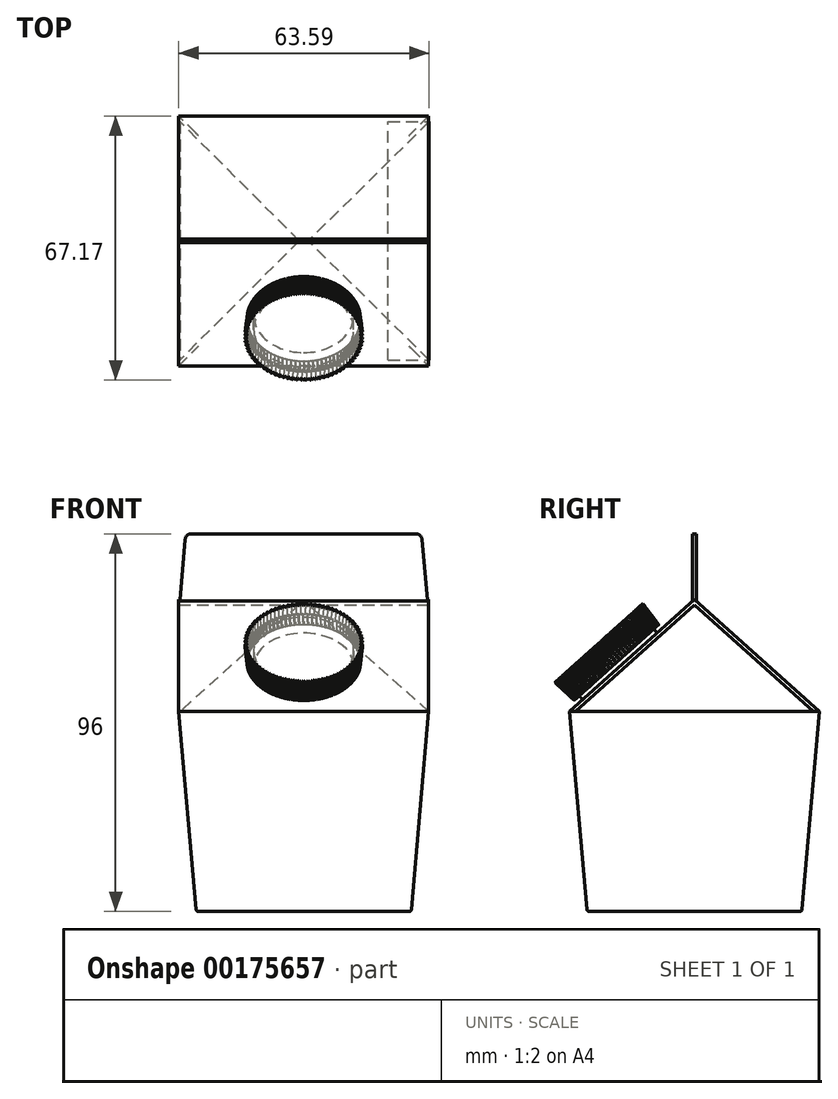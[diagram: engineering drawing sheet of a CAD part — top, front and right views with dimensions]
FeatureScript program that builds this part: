
annotation { "Feature Type Name" : "Feature", "Feature Type Description" : "" }
export const myFeature = defineFeature(function(context is Context, id is Id, definition is map)
    precondition{}
    {
        {
            var Q0;
            Q0=qCreatedBy(makeId("Top.planeOp"),FACE);
            var sketch = newSketch(context, id + "F0", { "sketchPlane" : qUnion([Q0])});
            skLineSegment(sketch, "E0.bottom", {"start": v(27.3, -27.3) * mm, "end": v(-27.3, -27.3) * mm});
            skLineSegment(sketch, "E0.top", {"start": v(27.3, 27.3) * mm, "end": v(-27.3, 27.3) * mm});
            skLineSegment(sketch, "E0.left", {"start": v(27.3, -27.3) * mm, "end": v(27.3, 27.3) * mm});
            skLineSegment(sketch, "E0.right", {"start": v(-27.3, -27.3) * mm, "end": v(-27.3, 27.3) * mm});
            skPoint(sketch, "E0.middle", {"position": v(0, 0) * mm});
            skSolve(sketch);
        }
        {
            var Q0;
            Q0=makeQuery(id+"F0.imprint","IMPRINT",FACE,{"disambiguationData":[TD([[makeQuery(id+"F0.imprint","IMPRINT",EDGE,{"derivedFrom":sQuery(id+"F0.wireOp",EDGE,"E0.bottom")}),-1.0]])]});
            extrude(context, id + "F1", {"entities" : qUnion([Q0]), "depth" : 50.8 * mm, "hasDraft" : true, "draftAngle" : 5 * degree});
        }
        {
            var Q0;
            Q0=qCreatedBy(makeId("Right.planeOp"),FACE);
            var sketch = newSketch(context, id + "F2", { "sketchPlane" : qUnion([Q0])});
            skLineSegment(sketch, "E1.0", {"start": v(-31.75, 50.8) * mm, "end": v(31.75, 50.8) * mm});
            skLineSegment(sketch, "E2", {"start": v(-27.4, 103.81) * mm, "end": v(78.6, 8.81) * mm, "construction": true});
            skLineSegment(sketch, "E3", {"start": v(0, -61.41) * mm, "end": v(0, 100.05) * mm, "construction": true});
            skLineSegment(sketch, "E4", {"start": v(31.75, 50.8) * mm, "end": v(0, 79.26) * mm, "construction": true});
            skPoint(sketch, "E4.endSnap0", {"position": v(0, 50.8) * mm});
            skLineSegment(sketch, "E5", {"start": v(0, 79.26) * mm, "end": v(-31.75, 50.8) * mm});
            skLineSegment(sketch, "E6", {"start": v(31.75, 50.8) * mm, "end": v(0, 79.26) * mm});
            skSolve(sketch);
        }
        {
            var Q0;
            Q0=makeQuery(id+"F2.imprint","IMPRINT",FACE,{"disambiguationData":[TD([[makeQuery(id+"F2.imprint","IMPRINT",EDGE,{"derivedFrom":sQuery(id+"F2.wireOp",EDGE,"E1.0")}),1.0]])]});
            extrude(context, id + "F3", {"entities" : qUnion([Q0]), "operationType" : NewBodyOperationType.ADD, "endBound" : BoundingType.SYMMETRIC, "depth" : 63.5 * mm});
        }
        {
            var Q0;
            Q0=makeQuery(id+"F3.opExtrude","CAP_FACE",FACE,{"disambiguationData":[OSD([sQuery(id+"F2.wireOp",EDGE,"E1.0"),sQuery(id+"F2.wireOp",EDGE,"E5"),sQuery(id+"F2.wireOp",EDGE,"E6")])],"isStart":false});
            var sketch = newSketch(context, id + "F4", { "sketchPlane" : qUnion([Q0])});
            skLineSegment(sketch, "E7", {"start": v(0, 28.77) * mm, "end": v(0, 80.29) * mm, "construction": true});
            skLineSegment(sketch, "E8.0", {"start": v(0, 77.96) * mm, "end": v(-30.3, 50.8) * mm});
            skLineSegment(sketch, "E8.1", {"start": v(30.3, 50.8) * mm, "end": v(0, 77.96) * mm});
            skLineSegment(sketch, "E9", {"start": v(-30.3, 50.8) * mm, "end": v(30.3, 50.8) * mm});
            skLineSegment(sketch, "E10", {"start": v(-17.16, 67.72) * mm, "end": v(-18, 68.66) * mm});
            skSolve(sketch);
        }
        {
            var Q0;
            Q0=makeQuery(id+"F4.imprint","IMPRINT",FACE,{"disambiguationData":[TD([[makeQuery(id+"F4.imprint","IMPRINT",EDGE,{"derivedFrom":sQuery(id+"F4.wireOp",EDGE,"E8.0")}),1.0]])]});
            extrude(context, id + "F5", {"entities" : qUnion([Q0]), "operationType" : NewBodyOperationType.REMOVE, "endBound" : BoundingType.THROUGH_ALL, "oppositeDirection" : true, "depth" : 25.4 * mm});
        }
        {
            var Q0;
            Q0=qCreatedBy(makeId("Front.planeOp"),FACE);
            var sketch = newSketch(context, id + "F6", { "sketchPlane" : qUnion([Q0])});
            skLineSegment(sketch, "E11.0", {"start": v(0, 79) * mm, "end": v(-31.59, 50.7) * mm});
            skLineSegment(sketch, "E11.1", {"start": v(31.84, 50.83) * mm, "end": v(0, 79) * mm});
            skLineSegment(sketch, "E12", {"start": v(-31.59, 50.7) * mm, "end": v(31.84, 50.83) * mm});
            skLineSegment(sketch, "E13", {"start": v(0, 0) * mm, "end": v(0, 79) * mm, "construction": true});
            skSolve(sketch);
        }
        {
            var Q0;
            Q0=makeQuery(id+"F6.imprint","IMPRINT",FACE,{"disambiguationData":[TD([[makeQuery(id+"F6.imprint","IMPRINT",EDGE,{"derivedFrom":sQuery(id+"F6.wireOp",EDGE,"E11.0")}),1.0]])]});
            var Q1;
            Q1=makeQuery(id+"F5.boolean.opBoolean","COPY",FACE,{"derivedFrom":makeQuery(id+"F5.opExtrude","SWEPT_FACE",FACE,{"disambiguationData":[OSD([sQuery(id+"F4.wireOp",EDGE,"E8.0")])]})});
            var Q2;
            Q2=makeQuery(id+"F1.opExtrude","SWEPT_BODY",BODY,{"disambiguationData":[OSD([sQuery(id+"F0.wireOp",EDGE,"E0.bottom"),sQuery(id+"F0.wireOp",EDGE,"E0.top"),sQuery(id+"F0.wireOp",EDGE,"E0.left"),sQuery(id+"F0.wireOp",EDGE,"E0.right")])]});
            extrude(context, id + "F7", {"entities" : qUnion([Q0]), "operationType" : NewBodyOperationType.ADD, "endBound" : BoundingType.UP_TO_SURFACE, "endBoundEntityFace" : qUnion([Q1]), "endBoundEntityBody" : qUnion([Q2]), "depth" : 63 * mm});
        }
        {
            var Q0;
            Q0=makeQuery(id+"F7.opExtrude","CAP_FACE",FACE,{"disambiguationData":[OSD([sQuery(id+"F6.wireOp",EDGE,"E11.0"),sQuery(id+"F6.wireOp",EDGE,"E11.1"),sQuery(id+"F6.wireOp",EDGE,"E12")])],"isStart":true});
            var Q1;
            Q1=makeQuery(id+"F5.boolean.opBoolean","COPY",FACE,{"derivedFrom":makeQuery(id+"F5.opExtrude","SWEPT_FACE",FACE,{"disambiguationData":[OSD([sQuery(id+"F4.wireOp",EDGE,"E8.1")])]})});
            extrude(context, id + "F8", {"entities" : qUnion([Q0]), "operationType" : NewBodyOperationType.ADD, "endBound" : BoundingType.UP_TO_SURFACE, "endBoundEntityFace" : qUnion([Q1]), "depth" : 25.4 * mm});
        }
        {
            var Q0;
            Q0=qCreatedBy(makeId("Front.planeOp"),FACE);
            var sketch = newSketch(context, id + "F9", { "sketchPlane" : qUnion([Q0])});
            skLineSegment(sketch, "E14.1", {"start": v(31.38, 79.25) * mm, "end": v(-31.48, 79.25) * mm});
            skLineSegment(sketch, "E15", {"start": v(-31.48, 79.25) * mm, "end": v(-30.14, 94.55) * mm});
            skLineSegment(sketch, "E16", {"start": v(-28.56, 96) * mm, "end": v(28.46, 96) * mm});
            skLineSegment(sketch, "E17", {"start": v(30.04, 94.55) * mm, "end": v(31.38, 79.25) * mm});
            skPoint(sketch, "E18.visualSharp", {"position": v(-30.02, 96) * mm});
            skArc(sketch, "E18.filletArc", {"start": v(-28.56, 96) * mm, "mid": v(-29.63, 95.58) * mm, "end": v(-30.14, 94.55) * mm});
            skPoint(sketch, "E19.visualSharp", {"position": v(29.91, 96) * mm});
            skArc(sketch, "E19.filletArc", {"start": v(30.04, 94.55) * mm, "mid": v(29.53, 95.58) * mm, "end": v(28.46, 96) * mm});
            skSolve(sketch);
        }
        {
            var Q0;
            Q0=makeQuery(id+"F9.imprint","IMPRINT",FACE,{"disambiguationData":[TD([[makeQuery(id+"F9.imprint","IMPRINT",EDGE,{"derivedFrom":sQuery(id+"F9.wireOp",EDGE,"E14.1")}),-1.0]])]});
            extrude(context, id + "F10", {"entities" : qUnion([Q0]), "operationType" : NewBodyOperationType.ADD, "endBound" : BoundingType.SYMMETRIC, "depth" : 0.97 * mm});
        }
        {
            var Q0;
            Q0=makeQuery(id+"F10.opExtrude","SWEPT_FACE",FACE,{"disambiguationData":[OSD([sQuery(id+"F9.wireOp",EDGE,"E14.1")])]});
            extrude(context, id + "F11", {"entities" : qUnion([Q0]), "operationType" : NewBodyOperationType.ADD, "depth" : 0.33 * mm});
        }
        {
            var Q0;
            Q0=makeQuery(id+"F1.opExtrude","CAP_FACE",FACE,{"disambiguationData":[OSD([sQuery(id+"F0.wireOp",EDGE,"E0.bottom"),sQuery(id+"F0.wireOp",EDGE,"E0.top"),sQuery(id+"F0.wireOp",EDGE,"E0.left"),sQuery(id+"F0.wireOp",EDGE,"E0.right")])],"isStart":true});
            fillet(context, id + "F12", {"entities" : qUnion([Q0]), "radius" : 0.64 * mm, "allowEdgeOverflow" : false});
        }
        {
            var Q0;
            Q0=makeQuery(id+"F3.opExtrude","SWEPT_FACE",FACE,{"disambiguationData":[OSD([sQuery(id+"F2.wireOp",EDGE,"E5")])]});
            var sketch = newSketch(context, id + "F13", { "sketchPlane" : qUnion([Q0])});
            skLineSegment(sketch, "E20", {"start": v(0, -101.08) * mm, "end": v(0, 122.86) * mm, "construction": true});
            skCircle(sketch, "E21", {"center": v(0, 27.48) * mm, "radius": 12.7 * mm});
            skCircle(sketch, "E22.0", {"center": v(0, 27.48) * mm, "radius": 14.29 * mm});
            skSolve(sketch);
        }
        {
            var Q0;
            Q0=makeQuery(id+"F13.imprint","IMPRINT",FACE,{"disambiguationData":[TD([[makeQuery(id+"F13.imprint","IMPRINT",EDGE,{"derivedFrom":sQuery(id+"F13.wireOp",EDGE,"E21")}),1.0]])]});
            extrude(context, id + "F14", {"entities" : qUnion([Q0]), "depth" : 5.36 * mm});
        }
        {
            var Q0;
            Q0=makeQuery(id+"F13.imprint","IMPRINT",FACE,{"disambiguationData":[TD([[makeQuery(id+"F13.imprint","IMPRINT",EDGE,{"derivedFrom":sQuery(id+"F13.wireOp",EDGE,"E21")}),-1.0]])]});
            var Q1;
            Q1=makeQuery(id+"F13.imprint","IMPRINT",FACE,{"disambiguationData":[TD([[makeQuery(id+"F13.imprint","IMPRINT",EDGE,{"derivedFrom":sQuery(id+"F13.wireOp",EDGE,"E21")}),1.0]])]});
            extrude(context, id + "F15", {"entities" : qUnion([Q0, Q1]), "depth" : 8 * mm, "hasDraft" : true, "draftAngle" : 5 * degree, "hasSecondDirection" : true, "secondDirectionOppositeDirection" : false, "secondDirectionDepth" : 1.32 * mm});
        }
        {
            var Q0;
            Q0=makeQuery(id+"F15.opExtrude","CAP_FACE",FACE,{"disambiguationData":[OSD([sQuery(id+"F13.wireOp",EDGE,"E22.0")])],"isStart":false});
            var sketch = newSketch(context, id + "F16", { "sketchPlane" : qUnion([Q0])});
            skLineSegment(sketch, "E23", {"start": v(0, 0) * mm, "end": v(0, 62.54) * mm, "construction": true});
            skLineSegment(sketch, "E24", {"start": v(0, 41.77) * mm, "end": v(-0.9, 43.09) * mm});
            skLineSegment(sketch, "E25", {"start": v(-0.9, 43.09) * mm, "end": v(0.9, 43.09) * mm});
            skLineSegment(sketch, "E26", {"start": v(0.9, 43.09) * mm, "end": v(0, 41.77) * mm});
            skSolve(sketch);
        }
        {
            var Q0;
            {var subQ0=sQuery(id+"F16.wireOp",EDGE,"E25");Q0=makeQuery(id+"F16.imprint","IMPRINT",FACE,{"disambiguationData":[TD([[makeQuery(id+"F16.imprint","IMPRINT",EDGE,{"derivedFrom":subQ0}),-1.0]])]});}
            var Q1;
            {var subQ0=sQuery(id+"F16.wireOp",EDGE,"E26");var subQ1=sQuery(id+"F16.wireOp",EDGE,"E24");var subQ2=makeQuery(id+"F16.imprint","INTERSECT",VERTEX,{"derivedFrom":[subQ1,subQ0]});Q1=makeQuery(id+"F16.imprint","IMPRINT",FACE,{"disambiguationData":[TD([[makeQuery(id+"F16.imprint","IMPRINT",EDGE,{"disambiguationData":[TD([[subQ2,-1.0]])],"derivedFrom":subQ1}),-1.0]])]});}
            extrude(context, id + "F17", {"entities" : qUnion([Q0, Q1]), "oppositeDirection" : true, "depth" : 6.93 * mm});
        }
        {
            var Q0;
            Q0=makeQuery(id+"F17.opExtrude","SWEPT_BODY",BODY,{"disambiguationData":[OSD([sQuery(id+"F16.wireOp",EDGE,"E24"),sQuery(id+"F16.wireOp",EDGE,"E25"),sQuery(id+"F16.wireOp",EDGE,"E26")])]});
            var Q1;
            Q1=makeQuery(id+"F15.opExtrude","CAP_EDGE",EDGE,{"disambiguationData":[OSD([sQuery(id+"F13.wireOp",EDGE,"E22.0")])],"isStart":false});
            circularPattern(context, id + "F18", {"operationType" : NewBodyOperationType.REMOVE, "entities" : qUnion([Q0]), "axis" : qUnion([Q1]), "angle" : 360 * degree, "instanceCount" : 80, "equalSpace" : true});
        }
    });
